# Revit family: LAMP_BAZZ AIR SYMMETRIC
name_source: partatom
category: Modelos genéricos
revit_build: Autodesk Revit 2018 (Build: 20190510_1515(x64)
units: mm (PartAtom-declared; Revit-internal decimal feet)

## family parameters
Anfitrión = Cara
Compartido = No
Corte con vacíos al cargar = No
Cota de conector redondo = Diámetro de uso
Puede alojar armadura = No
Punto de cálculo de habitación = No
Tipo de pieza = Normal

## types (8) — shared parameters
CRI = 80
Comentarios de tipo = Availability of tilting between 0º and 90º when placed in a project.
Dist. Rótula = 403 mm  [stored 1.32218 ft]
Elevación por defecto = 1219 mm
Fabricante = LAMP
Finish = Anodized matte black
Gear = Electronic
Height = 84 mm  [stored 0.275591 ft]
Installation instructions = http://www.lamp.es
Insulation class = I
LED Lifetime = 50.000 L80
Lamp = MID-POWER LED
Last update = 17/02/2022
Luminaire type = Outdoor -Recessed luminaire
MacAdam = <3
Manufacturer URL = http://www.lamp.es
Manufacturer country = Spain
Manufacturer name = LAMP
Model explanation = Availability of tilting between 0º and 90º when placed in a project.
Power Supply = 220-240V 50/60Hz
Product URL = http://www.lamp.es
Product datasheet = http://www.lamp.es
Protection rating = IP67 / IK10
Type = MID POWER SAMSUNG

## per-type parameters (varying)
| type | Descripción | Dimensions | Efficacy | Initial color | Initial intensity | Modelo | Photometric web file | Plum | Power | Product code | Weight |
| 2010LM 3000 1M | BAZZ AIR SYM 1M 2100 WW BK. | 1043x106x84 | 98 lm/W | 3000 K | 2010 lm | BZ1SF100LOSY830NB | Bazz air symmetric - base : 2010LM 3000 1M | 21 W | 19 W | BZ1SF100LOSY830NB | 3.73 kg |
| 2111LM 4000 1M | BAZZ AIR SYM 1M 2100 NW BK. | 1043x106x84 | 103 lm/W | 4000 K | 2111 lm | BZ1SF100LOSY840NB | Bazz air symmetric - base : 2111LM 4000 1M | 21 W | 19 W | BZ1SF100LOSY840NB | 3.73 kg |
| 3952LM 3000 1M | BAZZ AIR SYM 1M 4200 WW BK. | 1043x106x84 | 99 lm/W | 3000 K | 3952 lm | BZ1SF100MOSY830NB | Bazz air symmetric - base : 3952LM 3000 1M | 40 W | 37 W | BZ1SF100MOSY830NB | 3.73 kg |
| 4149LM 4000 1M | BAZZ AIR SYM 2M 4200 WW BK. | 1043x106x84 | 101 lm/W | 3000 K | 4020 lm | BZ1SF200LOSY830NB | Bazz air symmetric - base : 4149LM 4000 1M | 40 W | 38 W | BZ1SF200LOSY830NB | 6.70 kg |
| 4020LM 3000 2M | BAZZ AIR SYM 1M 4200 NW BK. | 1043x106x84 | 104 lm/W | 4000 K | 4149 lm | BZ1SF100MOSY840NB | Bazz air symmetric - base : 4020LM 3000 2M | 40 W | 37 W | BZ1SF100MOSY840NB | 3.73 kg |
| 4221LM 4000 2M | BAZZ AIR SYM 2M 4200 NW BK. | 2036x106x84 | 106 lm/W | 4000 K | 4221 lm | BZ1SF200LOSY840NB | Bazz air symmetric - base : 4221LM 4000 2M | 40 W | 38 W | BZ1SF200LOSY840NB | 6.70 kg |
| 7903LM 3000 2M | BAZZ AIR SYM 2M 8100 WW BK. | 2036x106x84 | 103 lm/W | 3000 K | 7903 lm | BZ1SF200MOSY830NB | Bazz air symmetric - base : 7903LM 3000 2M | 77 W | 75 W | BZ1SF200MOSY830NB | 6.70 kg |
| 8298LM 4000 2M | BAZZ AIR SYM 2M 8100 NW BK. | 2036x106x84 | 108 lm/W | 4000 K | 8298 lm | BZ1SF200MOSY840NB | Bazz air symmetric - base : 8298LM 4000 2M | 77 W | 75 W | BZ1SF200MOSY840NB | 6.70 kg |

note: [stored X ft] marks values corroborated as IEEE doubles in the binary element streams (Revit-internal decimal feet)

## geometry (parser evidence)
native form markers: Blend x2
no freeform markers — native parametric forms only
